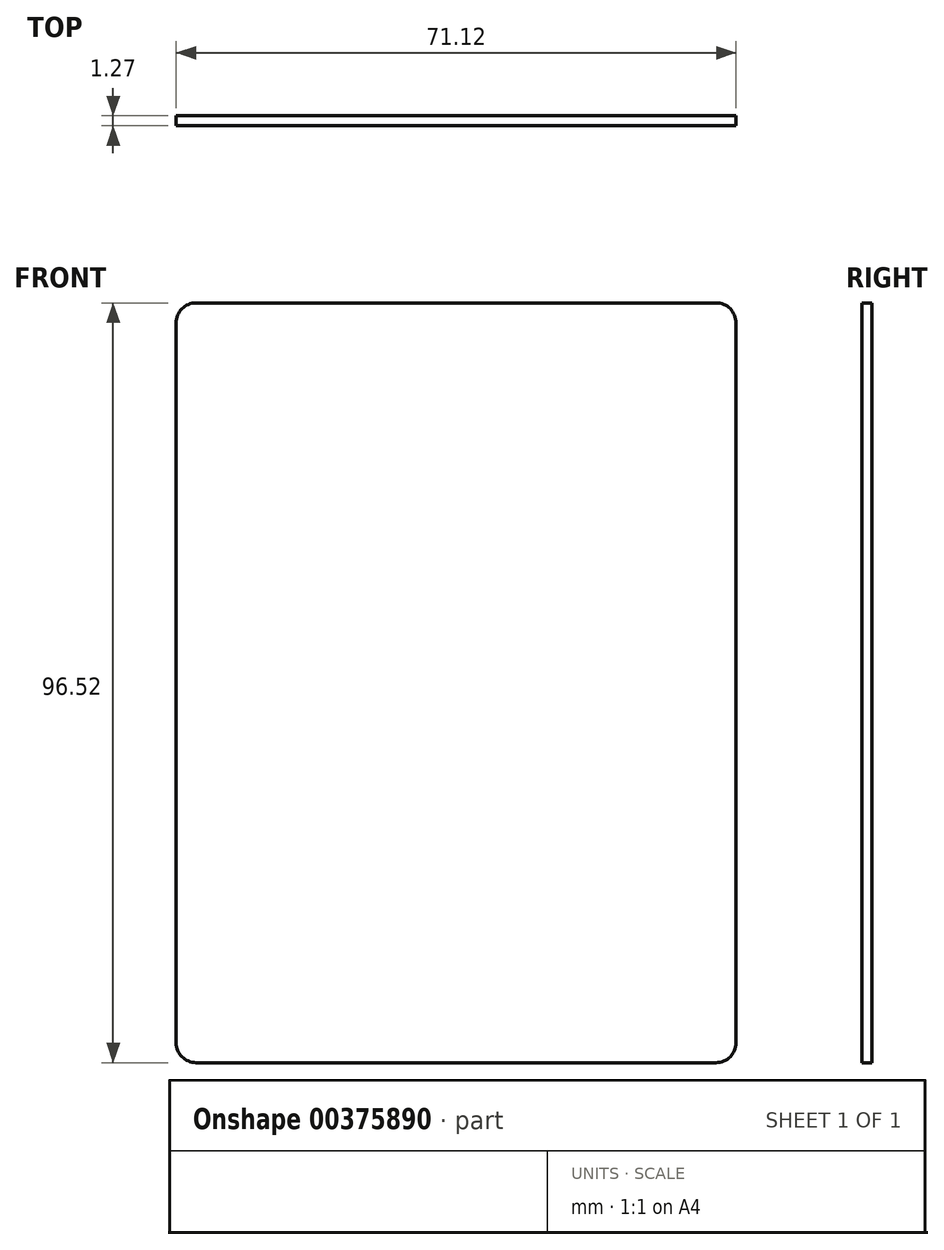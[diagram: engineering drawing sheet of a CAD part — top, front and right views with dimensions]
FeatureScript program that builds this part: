
annotation { "Feature Type Name" : "Feature", "Feature Type Description" : "" }
export const myFeature = defineFeature(function(context is Context, id is Id, definition is map)
    precondition{}
    {
        {
            var Q0;
            Q0=qCreatedBy(makeId("Front.planeOp"),FACE);
            var sketch = newSketch(context, id + "F0", { "sketchPlane" : qUnion([Q0])});
            skLineSegment(sketch, "E0.bottom", {"start": v(-42.74, 60.89) * mm, "end": v(23.3, 60.89) * mm});
            skLineSegment(sketch, "E0.top", {"start": v(-42.74, -35.63) * mm, "end": v(23.3, -35.63) * mm});
            skLineSegment(sketch, "E0.left", {"start": v(-45.28, 58.35) * mm, "end": v(-45.28, -33.1) * mm});
            skLineSegment(sketch, "E0.right", {"start": v(25.84, 58.35) * mm, "end": v(25.84, -33.1) * mm});
            skPoint(sketch, "E1.visualSharp", {"position": v(-45.28, -35.63) * mm});
            skArc(sketch, "E1.filletArc", {"start": v(-45.28, -33.1) * mm, "mid": v(-44.53, -34.89) * mm, "end": v(-42.74, -35.63) * mm});
            skPoint(sketch, "E2.visualSharp", {"position": v(25.84, -35.63) * mm});
            skArc(sketch, "E2.filletArc", {"start": v(23.3, -35.63) * mm, "mid": v(25.1, -34.89) * mm, "end": v(25.84, -33.1) * mm});
            skPoint(sketch, "E3.visualSharp", {"position": v(-45.28, 60.89) * mm});
            skArc(sketch, "E3.filletArc", {"start": v(-42.74, 60.89) * mm, "mid": v(-44.53, 60.14) * mm, "end": v(-45.28, 58.35) * mm});
            skPoint(sketch, "E4.visualSharp", {"position": v(25.84, 60.89) * mm});
            skArc(sketch, "E4.filletArc", {"start": v(25.84, 58.35) * mm, "mid": v(25.1, 60.14) * mm, "end": v(23.3, 60.89) * mm});
            skLineSegment(sketch, "E5", {"start": v(-33.85, 29.14) * mm, "end": v(14.41, 18.98) * mm});
            skSolve(sketch);
        }
        {
            var Q0;
            Q0=makeQuery(id+"F0.imprint","IMPRINT",FACE,{"disambiguationData":[TD([[makeQuery(id+"F0.imprint","IMPRINT",EDGE,{"derivedFrom":sQuery(id+"F0.wireOp",EDGE,"E0.bottom")}),-1.0]])]});
            extrude(context, id + "F1", {"entities" : qUnion([Q0]), "depth" : 1.27 * mm});
        }
    });
